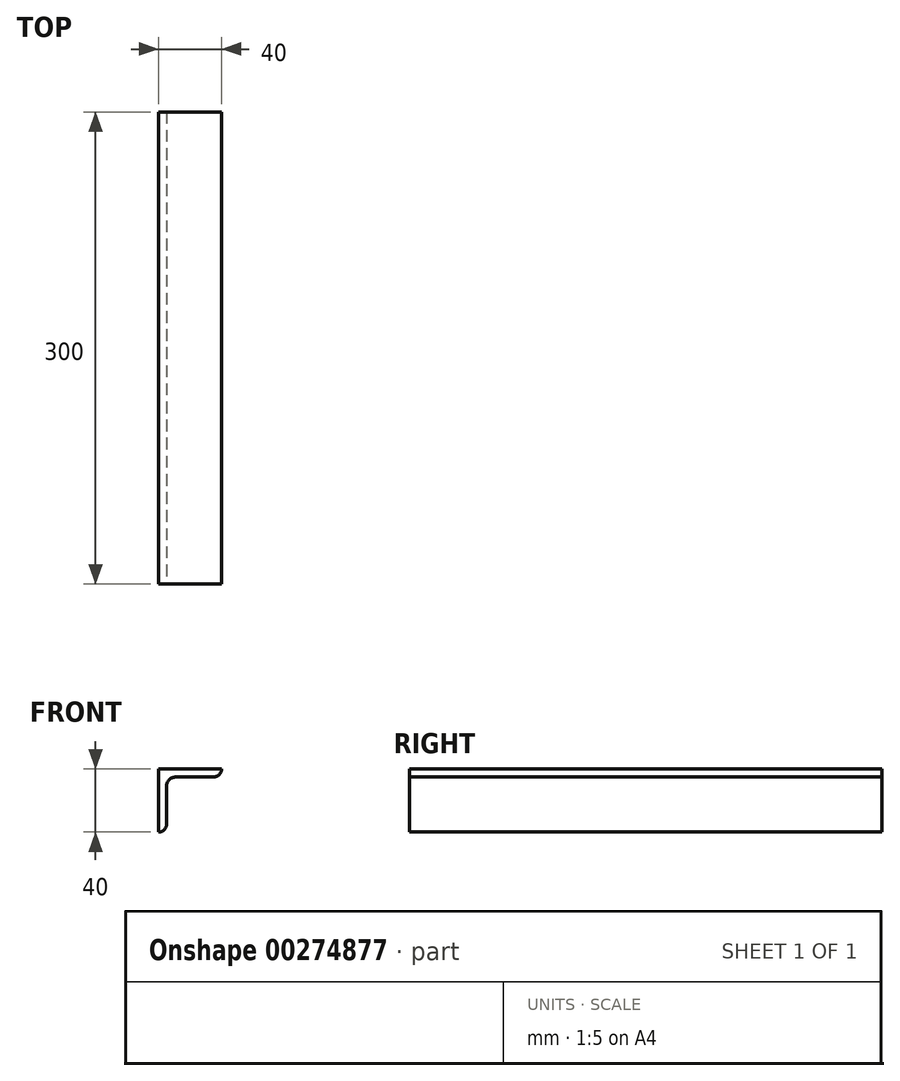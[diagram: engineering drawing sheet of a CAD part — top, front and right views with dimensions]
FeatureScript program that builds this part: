
annotation { "Feature Type Name" : "Feature", "Feature Type Description" : "" }
export const myFeature = defineFeature(function(context is Context, id is Id, definition is map)
    precondition{}
    {
        {
            var Q0;
            Q0=qCreatedBy(makeId("Front.planeOp"),FACE);
            var sketch = newSketch(context, id + "F0", { "sketchPlane" : qUnion([Q0])});
            skLineSegment(sketch, "E0", {"start": v(0, 0) * mm, "end": v(0, 40) * mm});
            skLineSegment(sketch, "E1", {"start": v(0, 40) * mm, "end": v(40, 40) * mm});
            skLineSegment(sketch, "E2.0", {"start": v(5, 5) * mm, "end": v(5, 29) * mm});
            skLineSegment(sketch, "E3.0", {"start": v(11, 35) * mm, "end": v(35, 35) * mm});
            skLineSegment(sketch, "E4", {"start": v(40, 40) * mm, "end": v(40, 40) * mm});
            skLineSegment(sketch, "E5", {"start": v(-0.05, 0) * mm, "end": v(0, 0) * mm});
            skArc(sketch, "E6.filletArc", {"start": v(11, 35) * mm, "mid": v(6.76, 33.24) * mm, "end": v(5, 29) * mm});
            skPoint(sketch, "E7.visualSharp", {"position": v(40, 35) * mm});
            skArc(sketch, "E7.filletArc", {"start": v(35, 35) * mm, "mid": v(38.54, 36.46) * mm, "end": v(40, 40) * mm});
            skPoint(sketch, "E8.visualSharp", {"position": v(5, -0.05) * mm});
            skArc(sketch, "E8.filletArc", {"start": v(-0.05, 0) * mm, "mid": v(3.52, 1.45) * mm, "end": v(5, 5) * mm});
            skSolve(sketch);
        }
        {
            var Q0;
            {var subQ1=sQuery(id+"F0.wireOp",EDGE,"E1");Q0=makeQuery(id+"F0.imprint","IMPRINT",FACE,{"disambiguationData":[TD([[makeQuery(id+"F0.imprint","IMPRINT",EDGE,{"derivedFrom":subQ1}),-1.0]])]});}
            extrude(context, id + "F1", {"entities" : qUnion([Q0]), "oppositeDirection" : true, "depth" : 300 * mm});
        }
        {
            var Q0;
            Q0=makeQuery(id+"F1.opExtrude","SWEPT_FACE",FACE,{"disambiguationData":[OSD([sQuery(id+"F0.wireOp",EDGE,"E1")])]});
            var sketch = newSketch(context, id + "F10", { "sketchPlane" : qUnion([Q0])});
            skCircle(sketch, "E9", {"center": v(10, 10) * mm, "radius": 4 * mm});
            skSolve(sketch);
        }
        {
            var Q0;
            Q0=makeQuery(id+"F1.opExtrude","SWEPT_FACE",FACE,{"disambiguationData":[OSD([sQuery(id+"F0.wireOp",EDGE,"E0")])]});
            var sketch = newSketch(context, id + "F11", { "sketchPlane" : qUnion([Q0])});
            skCircle(sketch, "E10", {"center": v(-30, 30) * mm, "radius": 4 * mm});
            skSolve(sketch);
        }
        {
            var Q0;
            Q0=qCreatedBy(makeId("Front.planeOp"),FACE);
            cPlane(context, id + "F2", {"entities" : qUnion([Q0]), "cplaneType" : CPlaneType.OFFSET, "offset" : 150 * mm, "oppositeDirection" : true, "width" : 150 * mm, "height" : 150 * mm});
        }
    });
